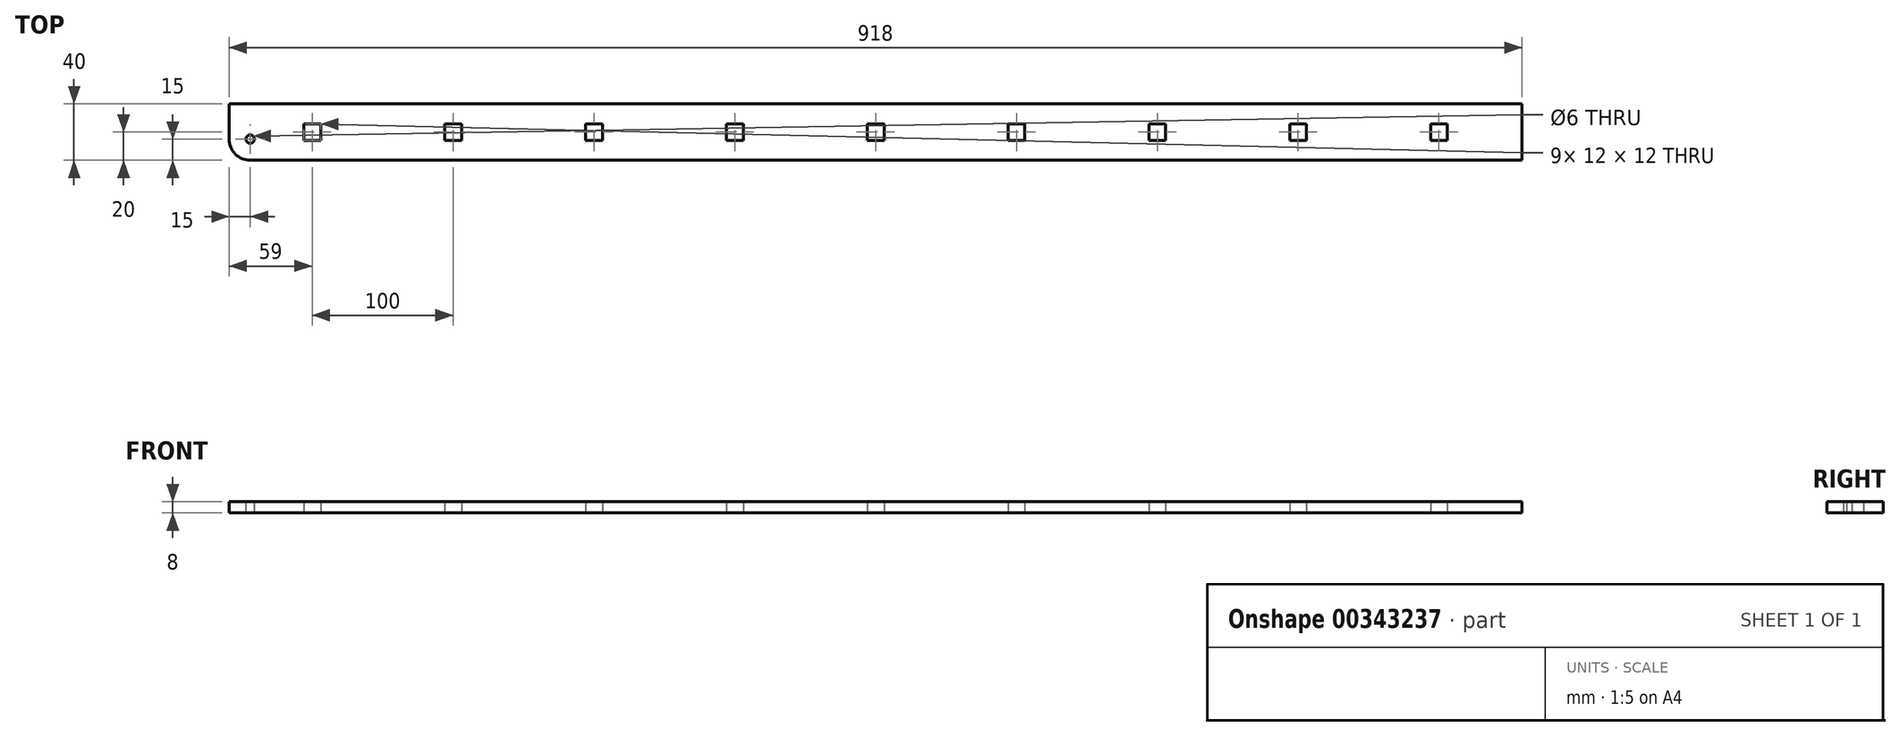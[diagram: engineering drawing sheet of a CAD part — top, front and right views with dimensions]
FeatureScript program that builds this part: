
annotation { "Feature Type Name" : "Feature", "Feature Type Description" : "" }
export const myFeature = defineFeature(function(context is Context, id is Id, definition is map)
    precondition{}
    {
        {
            var Q0;
            Q0=qCreatedBy(makeId("Top.planeOp"),FACE);
            var sketch = newSketch(context, id + "F0", { "sketchPlane" : qUnion([Q0])});
            skLineSegment(sketch, "E0.bottom", {"start": v(459, 20) * mm, "end": v(-459, 20) * mm});
            skLineSegment(sketch, "E0.top", {"start": v(459, -20) * mm, "end": v(-444, -20) * mm});
            skLineSegment(sketch, "E0.left", {"start": v(459, 20) * mm, "end": v(459, -20) * mm});
            skLineSegment(sketch, "E0.right", {"start": v(-459, 20) * mm, "end": v(-459, -5) * mm});
            skPoint(sketch, "E0.middle", {"position": v(0, 0) * mm});
            skLineSegment(sketch, "E1.0", {"start": v(-444, 30) * mm, "end": v(-444, -20) * mm, "construction": true});
            skLineSegment(sketch, "E2.0", {"start": v(440, -5) * mm, "end": v(-440, -5) * mm, "construction": true});
            skPoint(sketch, "E3", {"position": v(-444, -5) * mm});
            skArc(sketch, "E4", {"start": v(-444, -20) * mm, "mid": v(-454.6, -15.6) * mm, "end": v(-459, -5) * mm});
            skPoint(sketch, "E5.orphan", {"position": v(-459, -20) * mm});
            skLineSegment(sketch, "E6.bottom", {"start": v(6, 6) * mm, "end": v(-6, 6) * mm});
            skLineSegment(sketch, "E6.top", {"start": v(6, -6) * mm, "end": v(-6, -6) * mm});
            skLineSegment(sketch, "E6.left", {"start": v(6, 6) * mm, "end": v(6, -6) * mm});
            skLineSegment(sketch, "E6.right", {"start": v(-6, 6) * mm, "end": v(-6, -6) * mm});
            skPoint(sketch, "E7.1.0.0", {"position": v(100, 0) * mm});
            skLineSegment(sketch, "E7.1.0.1", {"start": v(106, 6) * mm, "end": v(94, 6) * mm});
            skLineSegment(sketch, "E7.1.0.2", {"start": v(106, -6) * mm, "end": v(94, -6) * mm});
            skLineSegment(sketch, "E7.1.0.3", {"start": v(106, 6) * mm, "end": v(106, -6) * mm});
            skLineSegment(sketch, "E7.1.0.4", {"start": v(94, 6) * mm, "end": v(94, -6) * mm});
            skPoint(sketch, "E7.1.0.5", {"position": v(100, 0) * mm});
            skPoint(sketch, "E7.2.0.0", {"position": v(200, 0) * mm});
            skLineSegment(sketch, "E7.2.0.1", {"start": v(206, 6) * mm, "end": v(194, 6) * mm});
            skLineSegment(sketch, "E7.2.0.2", {"start": v(206, -6) * mm, "end": v(194, -6) * mm});
            skLineSegment(sketch, "E7.2.0.3", {"start": v(206, 6) * mm, "end": v(206, -6) * mm});
            skLineSegment(sketch, "E7.2.0.4", {"start": v(194, 6) * mm, "end": v(194, -6) * mm});
            skPoint(sketch, "E7.2.0.5", {"position": v(200, 0) * mm});
            skPoint(sketch, "E7.3.0.0", {"position": v(300, 0) * mm});
            skLineSegment(sketch, "E7.3.0.1", {"start": v(306, 6) * mm, "end": v(294, 6) * mm});
            skLineSegment(sketch, "E7.3.0.2", {"start": v(306, -6) * mm, "end": v(294, -6) * mm});
            skLineSegment(sketch, "E7.3.0.3", {"start": v(306, 6) * mm, "end": v(306, -6) * mm});
            skLineSegment(sketch, "E7.3.0.4", {"start": v(294, 6) * mm, "end": v(294, -6) * mm});
            skPoint(sketch, "E7.3.0.5", {"position": v(300, 0) * mm});
            skPoint(sketch, "E7.4.0.0", {"position": v(400, 0) * mm});
            skLineSegment(sketch, "E7.4.0.1", {"start": v(406, 6) * mm, "end": v(394, 6) * mm});
            skLineSegment(sketch, "E7.4.0.2", {"start": v(406, -6) * mm, "end": v(394, -6) * mm});
            skLineSegment(sketch, "E7.4.0.3", {"start": v(406, 6) * mm, "end": v(406, -6) * mm});
            skLineSegment(sketch, "E7.4.0.4", {"start": v(394, 6) * mm, "end": v(394, -6) * mm});
            skPoint(sketch, "E7.4.0.5", {"position": v(400, 0) * mm});
            skLineSegment(sketch, "E7.direction1", {"start": v(-6, -6) * mm, "end": v(94, -6) * mm, "construction": true});
            skLineSegment(sketch, "E8.1.0.0", {"start": v(-106, 6) * mm, "end": v(-106, -6) * mm});
            skLineSegment(sketch, "E8.1.0.1", {"start": v(-94, 6) * mm, "end": v(-106, 6) * mm});
            skPoint(sketch, "E8.1.0.2", {"position": v(-100, 0) * mm});
            skLineSegment(sketch, "E8.1.0.3", {"start": v(-94, 6) * mm, "end": v(-94, -6) * mm});
            skLineSegment(sketch, "E8.1.0.4", {"start": v(-94, -6) * mm, "end": v(-106, -6) * mm});
            skPoint(sketch, "E8.1.0.5", {"position": v(-100, 0) * mm});
            skLineSegment(sketch, "E8.2.0.0", {"start": v(-206, 6) * mm, "end": v(-206, -6) * mm});
            skLineSegment(sketch, "E8.2.0.1", {"start": v(-194, 6) * mm, "end": v(-206, 6) * mm});
            skPoint(sketch, "E8.2.0.2", {"position": v(-200, 0) * mm});
            skLineSegment(sketch, "E8.2.0.3", {"start": v(-194, 6) * mm, "end": v(-194, -6) * mm});
            skLineSegment(sketch, "E8.2.0.4", {"start": v(-194, -6) * mm, "end": v(-206, -6) * mm});
            skPoint(sketch, "E8.2.0.5", {"position": v(-200, 0) * mm});
            skLineSegment(sketch, "E8.3.0.0", {"start": v(-306, 6) * mm, "end": v(-306, -6) * mm});
            skLineSegment(sketch, "E8.3.0.1", {"start": v(-294, 6) * mm, "end": v(-306, 6) * mm});
            skPoint(sketch, "E8.3.0.2", {"position": v(-300, 0) * mm});
            skLineSegment(sketch, "E8.3.0.3", {"start": v(-294, 6) * mm, "end": v(-294, -6) * mm});
            skLineSegment(sketch, "E8.3.0.4", {"start": v(-294, -6) * mm, "end": v(-306, -6) * mm});
            skPoint(sketch, "E8.3.0.5", {"position": v(-300, 0) * mm});
            skLineSegment(sketch, "E8.4.0.0", {"start": v(-406, 6) * mm, "end": v(-406, -6) * mm});
            skLineSegment(sketch, "E8.4.0.1", {"start": v(-394, 6) * mm, "end": v(-406, 6) * mm});
            skPoint(sketch, "E8.4.0.2", {"position": v(-400, 0) * mm});
            skLineSegment(sketch, "E8.4.0.3", {"start": v(-394, 6) * mm, "end": v(-394, -6) * mm});
            skLineSegment(sketch, "E8.4.0.4", {"start": v(-394, -6) * mm, "end": v(-406, -6) * mm});
            skPoint(sketch, "E8.4.0.5", {"position": v(-400, 0) * mm});
            skLineSegment(sketch, "E8.direction1", {"start": v(-6, -6) * mm, "end": v(-106, -6) * mm, "construction": true});
            skSolve(sketch);
        }
        {
            var Q0;
            Q0=makeQuery(id+"F0.imprint","IMPRINT",FACE,{"disambiguationData":[TD([[makeQuery(id+"F0.imprint","IMPRINT",EDGE,{"derivedFrom":sQuery(id+"F0.wireOp",EDGE,"E0.bottom")}),1.0]])]});
            extrude(context, id + "F1", {"entities" : qUnion([Q0]), "endBound" : BoundingType.SYMMETRIC, "depth" : 8 * mm});
        }
        {
            var Q0;
            Q0=sQuery(id+"F0.wireOp",VERTEX,"E3");
            var Q1;
            Q1=makeQuery(id+"F1.opExtrude","SWEPT_BODY",BODY,{"disambiguationData":[OSD([sQuery(id+"F0.wireOp",EDGE,"E0.bottom"),sQuery(id+"F0.wireOp",EDGE,"E0.top"),sQuery(id+"F0.wireOp",EDGE,"E0.left"),sQuery(id+"F0.wireOp",EDGE,"E0.right")])]});
            hole(context, id + "F2", {"style" : HoleStyle.SIMPLE, "endStyle" : HoleEndStyle.THROUGH, "holeDiameter" : 6 * mm, "isTappedThrough" : true, "tappedDepth" : 6 * mm, "tapClearance" : 3, "startFromSketch" : true, "locations" : qUnion([Q0]), "scope" : qUnion([Q1])});
        }
        {
            var Q0;
            Q0=sQuery(id+"F0.wireOp",VERTEX,"E3");
            var Q1;
            Q1=makeQuery(id+"F1.opExtrude","SWEPT_BODY",BODY,{"disambiguationData":[OSD([sQuery(id+"F0.wireOp",EDGE,"E0.bottom"),sQuery(id+"F0.wireOp",EDGE,"E0.top"),sQuery(id+"F0.wireOp",EDGE,"E0.left"),sQuery(id+"F0.wireOp",EDGE,"E0.right")])]});
            hole(context, id + "F3", {"style" : HoleStyle.SIMPLE, "endStyle" : HoleEndStyle.THROUGH, "oppositeDirection" : true, "holeDiameter" : 6 * mm, "isTappedThrough" : true, "tappedDepth" : 6 * mm, "tapClearance" : 3, "startFromSketch" : true, "locations" : qUnion([Q0]), "scope" : qUnion([Q1])});
        }
    });
